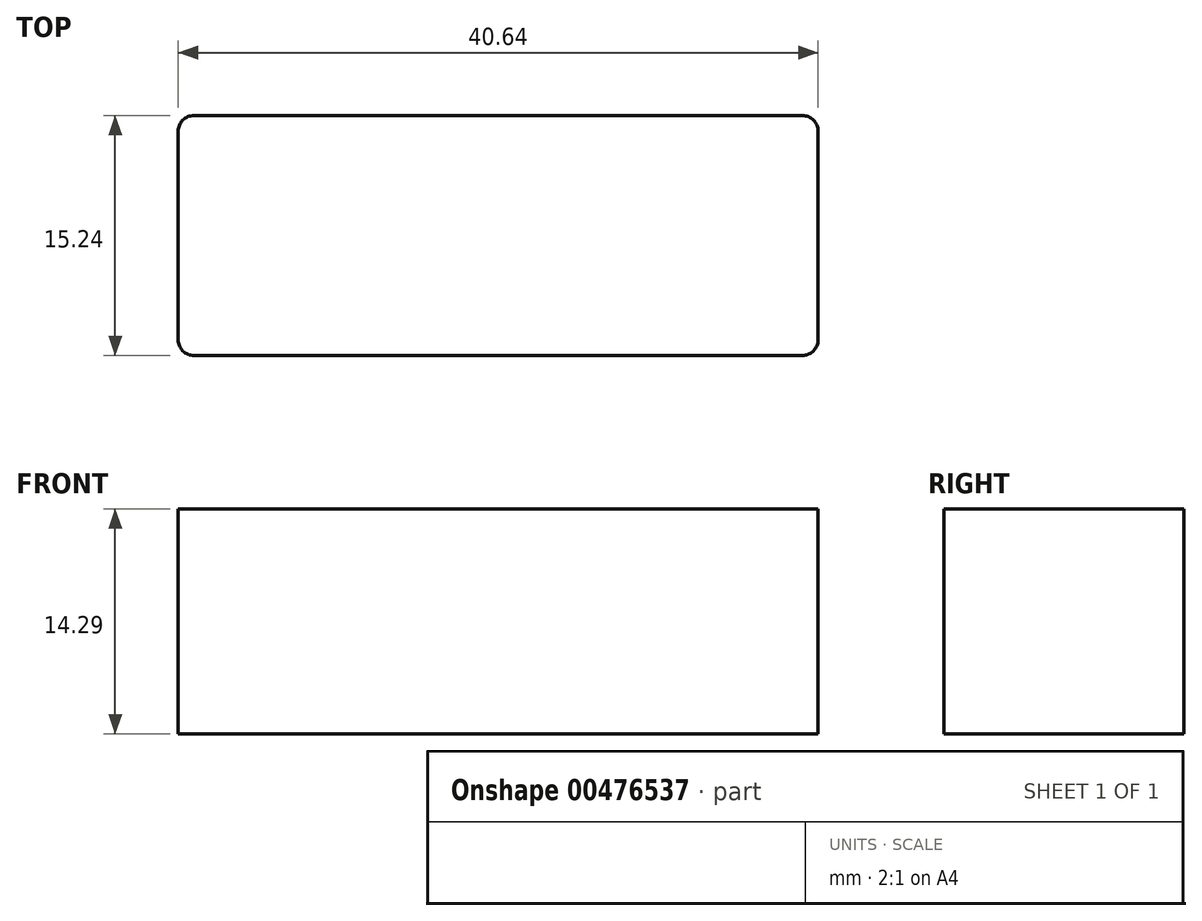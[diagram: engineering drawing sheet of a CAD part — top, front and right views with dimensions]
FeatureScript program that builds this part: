
annotation { "Feature Type Name" : "Feature", "Feature Type Description" : "" }
export const myFeature = defineFeature(function(context is Context, id is Id, definition is map)
    precondition{}
    {
        {
            var Q0;
            Q0=qCreatedBy(makeId("Top.planeOp"),FACE);
            var sketch = newSketch(context, id + "F0", { "sketchPlane" : qUnion([Q0])});
            skLineSegment(sketch, "E0.bottom", {"start": v(20.32, 7.62) * mm, "end": v(-20.32, 7.62) * mm});
            skLineSegment(sketch, "E0.top", {"start": v(20.32, -7.62) * mm, "end": v(-20.32, -7.62) * mm});
            skLineSegment(sketch, "E0.left", {"start": v(20.32, 7.62) * mm, "end": v(20.32, -7.62) * mm});
            skLineSegment(sketch, "E0.right", {"start": v(-20.32, 7.62) * mm, "end": v(-20.32, -7.62) * mm});
            skPoint(sketch, "E0.middle", {"position": v(0, 0) * mm});
            skSolve(sketch);
        }
        {
            var Q0;
            Q0=makeQuery(id+"F0.imprint","IMPRINT",FACE,{"disambiguationData":[TD([[makeQuery(id+"F0.imprint","IMPRINT",EDGE,{"derivedFrom":sQuery(id+"F0.wireOp",EDGE,"E0.bottom")}),1.0]])]});
            extrude(context, id + "F1", {"entities" : qUnion([Q0]), "depth" : 14.29 * mm});
        }
        {
            var Q0;
            Q0=makeQuery(id+"F1.opExtrude","SWEPT_EDGE",EDGE,{"disambiguationData":[OSD([sQuery(id+"F0.wireOp",EDGE,"E0.top"),sQuery(id+"F0.wireOp",EDGE,"E0.left")])]});
            var Q1;
            Q1=makeQuery(id+"F1.opExtrude","SWEPT_EDGE",EDGE,{"disambiguationData":[OSD([sQuery(id+"F0.wireOp",EDGE,"E0.top"),sQuery(id+"F0.wireOp",EDGE,"E0.right")])]});
            var Q2;
            Q2=makeQuery(id+"F1.opExtrude","SWEPT_EDGE",EDGE,{"disambiguationData":[OSD([sQuery(id+"F0.wireOp",EDGE,"E0.bottom"),sQuery(id+"F0.wireOp",EDGE,"E0.left")])]});
            var Q3;
            Q3=makeQuery(id+"F1.opExtrude","SWEPT_EDGE",EDGE,{"disambiguationData":[OSD([sQuery(id+"F0.wireOp",EDGE,"E0.bottom"),sQuery(id+"F0.wireOp",EDGE,"E0.right")])]});
            fillet(context, id + "F2", {"entities" : qUnion([Q0, Q1, Q2, Q3]), "radius" : 1 * mm, "tangentPropagation" : true, "allowEdgeOverflow" : false});
        }
    });
